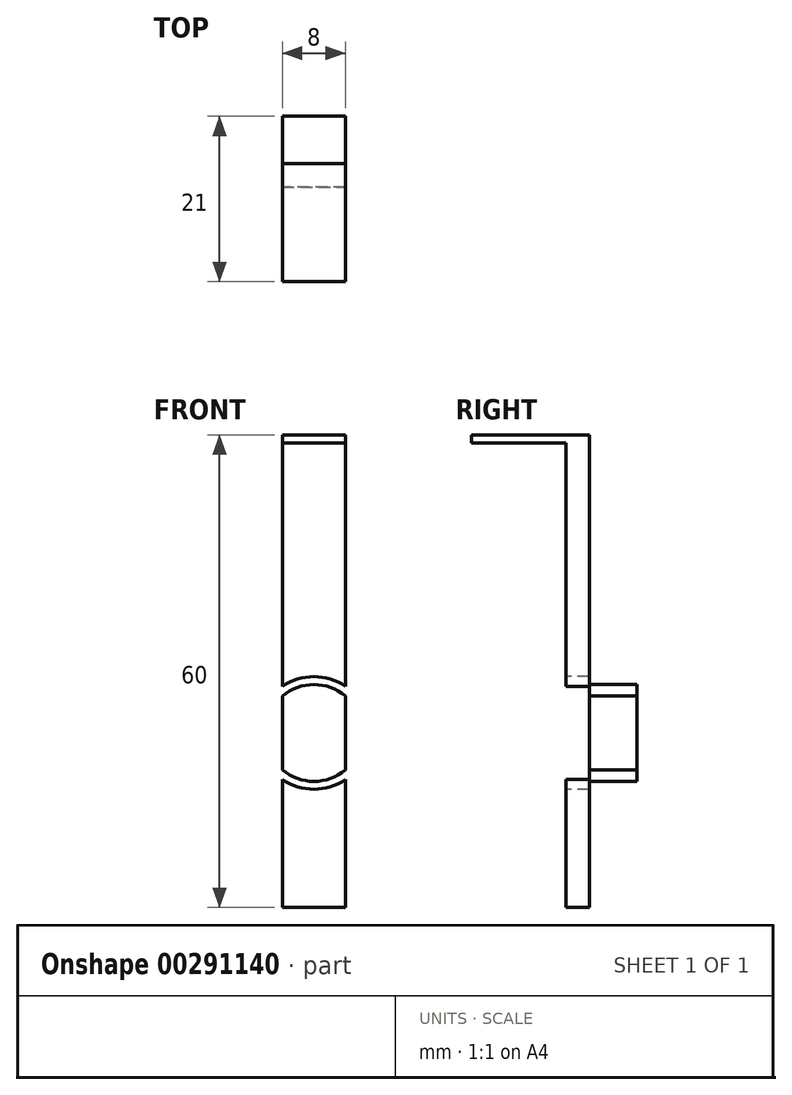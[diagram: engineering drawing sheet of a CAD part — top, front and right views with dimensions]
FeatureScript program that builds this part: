
annotation { "Feature Type Name" : "Feature", "Feature Type Description" : "" }
export const myFeature = defineFeature(function(context is Context, id is Id, definition is map)
    precondition{}
    {
        {
            var Q0;
            Q0=qCreatedBy(makeId("Front.planeOp"),FACE);
            var sketch = newSketch(context, id + "F0", { "sketchPlane" : qUnion([Q0])});
            skLineSegment(sketch, "E0.bottom", {"start": v(-14.75, 0) * mm, "end": v(-22.75, 0) * mm});
            skLineSegment(sketch, "E0.top", {"start": v(-14.75, 60) * mm, "end": v(-22.75, 60) * mm});
            skLineSegment(sketch, "E0.left", {"start": v(-14.75, 0) * mm, "end": v(-14.75, 60) * mm});
            skLineSegment(sketch, "E0.right", {"start": v(-22.75, 0) * mm, "end": v(-22.75, 60) * mm});
            skCircle(sketch, "E1", {"center": v(-18.75, 22.15) * mm, "radius": 7.15 * mm});
            skPoint(sketch, "E1.centerSnap0", {"position": v(-18.75, 0) * mm});
            skSolve(sketch);
        }
        {
            var Q0;
            {var subQ0=sQuery(id+"F0.wireOp",EDGE,"E0.top");Q0=makeQuery(id+"F0.imprint","IMPRINT",FACE,{"disambiguationData":[TD([[makeQuery(id+"F0.imprint","IMPRINT",EDGE,{"derivedFrom":subQ0}),1.0]])]});}
            var Q1;
            {var subQ0=sQuery(id+"F0.wireOp",EDGE,"E1");var subQ1=sQuery(id+"F0.wireOp",EDGE,"E0.left");var subQ2=makeQuery(id+"F0.imprint","INTERSECT",VERTEX,{"disambiguationData":[OD(0.0)],"derivedFrom":[subQ1,subQ0]});Q1=makeQuery(id+"F0.imprint","IMPRINT",FACE,{"disambiguationData":[TD([[makeQuery(id+"F0.imprint","IMPRINT",EDGE,{"disambiguationData":[TD([[subQ2,-1.0]])],"derivedFrom":subQ1}),1.0]])]});}
            var Q2;
            {var subQ0=sQuery(id+"F0.wireOp",EDGE,"E0.bottom");Q2=makeQuery(id+"F0.imprint","IMPRINT",FACE,{"disambiguationData":[TD([[makeQuery(id+"F0.imprint","IMPRINT",EDGE,{"derivedFrom":subQ0}),-1.0]])]});}
            extrude(context, id + "F1", {"entities" : qUnion([Q0, Q1, Q2]), "oppositeDirection" : true, "depth" : 3 * mm});
        }
        {
            var Q0;
            Q0=makeQuery(id+"F1.opExtrude","CAP_FACE",FACE,{"disambiguationData":[OSD([sQuery(id+"F0.wireOp",EDGE,"E0.bottom"),sQuery(id+"F0.wireOp",EDGE,"E0.top"),sQuery(id+"F0.wireOp",EDGE,"E0.left"),sQuery(id+"F0.wireOp",EDGE,"E0.right")])],"isStart":false});
            var sketch = newSketch(context, id + "F2", { "sketchPlane" : qUnion([Q0])});
            skLineSegment(sketch, "E2.0", {"start": v(14.75, 0) * mm, "end": v(22.75, 0) * mm});
            skLineSegment(sketch, "E2.1", {"start": v(14.75, 60) * mm, "end": v(22.75, 60) * mm});
            skLineSegment(sketch, "E2.2", {"start": v(14.75, 0) * mm, "end": v(14.75, 16.22) * mm});
            skLineSegment(sketch, "E2.3", {"start": v(22.75, 0) * mm, "end": v(22.75, 16.22) * mm});
            skPoint(sketch, "E2.5", {"position": v(18.75, 0) * mm});
            skArc(sketch, "E3", {"start": v(14.75, 26.82) * mm, "mid": v(18.75, 28.3) * mm, "end": v(22.75, 26.82) * mm});
            skArc(sketch, "E4", {"start": v(22.75, 26.82) * mm, "mid": v(24.9, 22.15) * mm, "end": v(22.75, 17.48) * mm});
            skArc(sketch, "E5", {"start": v(22.75, 17.48) * mm, "mid": v(18.75, 16) * mm, "end": v(14.75, 17.48) * mm});
            skArc(sketch, "E6", {"start": v(14.75, 17.48) * mm, "mid": v(12.6, 22.15) * mm, "end": v(14.75, 26.82) * mm});
            skLineSegment(sketch, "E7", {"start": v(14.75, 16.22) * mm, "end": v(14.75, 17.48) * mm});
            skLineSegment(sketch, "E8", {"start": v(22.75, 16.22) * mm, "end": v(22.75, 17.48) * mm});
            skArc(sketch, "E9", {"start": v(22.75, 28.08) * mm, "mid": v(25.9, 22.15) * mm, "end": v(22.75, 16.22) * mm});
            skArc(sketch, "E10", {"start": v(14.75, 28.08) * mm, "mid": v(18.75, 29.3) * mm, "end": v(22.75, 28.08) * mm});
            skLineSegment(sketch, "E11", {"start": v(14.75, 28.08) * mm, "end": v(14.75, 60) * mm});
            skLineSegment(sketch, "E12", {"start": v(14.75, 26.82) * mm, "end": v(14.75, 28.08) * mm});
            skLineSegment(sketch, "E13", {"start": v(22.75, 26.82) * mm, "end": v(22.75, 28.08) * mm});
            skLineSegment(sketch, "E14", {"start": v(22.75, 28.08) * mm, "end": v(22.75, 60) * mm});
            skLineSegment(sketch, "E15", {"start": v(22.75, 17.48) * mm, "end": v(22.75, 26.82) * mm});
            skArc(sketch, "E16", {"start": v(22.75, 16.22) * mm, "mid": v(18.75, 15) * mm, "end": v(14.75, 16.22) * mm});
            skArc(sketch, "E17", {"start": v(14.75, 16.22) * mm, "mid": v(11.6, 22.15) * mm, "end": v(14.75, 28.08) * mm});
            skLineSegment(sketch, "E18", {"start": v(14.75, 17.48) * mm, "end": v(14.75, 26.82) * mm});
            skLineSegment(sketch, "E19", {"start": v(22.75, 59) * mm, "end": v(14.75, 59) * mm});
            skSolve(sketch);
        }
        {
            var Q0;
            Q0=makeQuery(id+"F2.imprint","IMPRINT",FACE,{"disambiguationData":[TD([[makeQuery(id+"F2.imprint","IMPRINT",EDGE,{"derivedFrom":sQuery(id+"F2.wireOp",EDGE,"E3")}),1.0]])]});
            var Q1;
            Q1=makeQuery(id+"F2.imprint","IMPRINT",FACE,{"disambiguationData":[TD([[makeQuery(id+"F2.imprint","IMPRINT",EDGE,{"derivedFrom":sQuery(id+"F2.wireOp",EDGE,"E5")}),1.0]])]});
            var Q2;
            Q2=sQuery(id+"F2.wireOp",EDGE,"E8");
            var Q3;
            Q3=sQuery(id+"F2.wireOp",EDGE,"E16");
            var Q4;
            Q4=sQuery(id+"F2.wireOp",EDGE,"E5");
            var Q5;
            Q5=sQuery(id+"F2.wireOp",EDGE,"E7");
            var Q6;
            Q6=sQuery(id+"F2.wireOp",EDGE,"E10");
            var Q7;
            Q7=sQuery(id+"F2.wireOp",EDGE,"E3");
            var Q8;
            Q8=sQuery(id+"F2.wireOp",EDGE,"E12");
            var Q9;
            Q9=sQuery(id+"F2.wireOp",EDGE,"E13");
            extrude(context, id + "F3", {"entities" : qUnion([Q0, Q1]), "operationType" : NewBodyOperationType.ADD, "surfaceEntities" : qUnion([Q2, Q3, Q4, Q5, Q6, Q7, Q8, Q9]), "depth" : 6 * mm});
        }
        {
            var Q0;
            {var subQ0=sQuery(id+"F2.wireOp",EDGE,"E2.1");Q0=makeQuery(id+"F2.imprint","IMPRINT",FACE,{"disambiguationData":[TD([[makeQuery(id+"F2.imprint","IMPRINT",EDGE,{"derivedFrom":subQ0}),-1.0]])]});}
            extrude(context, id + "F4", {"entities" : qUnion([Q0]), "operationType" : NewBodyOperationType.ADD, "oppositeDirection" : true, "depth" : 15 * mm});
        }
    });
